# Revit family: Porecz_uchylna_dla_niepelnosprawnych_800 mm stal szlachetna matowa
name_source: partatom
category: Furniture
units: mm (PartAtom-declared; Revit-internal decimal feet)

## family parameters
Always vertical = Yes
Cut with Voids When Loaded = No
Host = Wall
Room Calculation Point = No
Shared = No

## types (1)
- S32UUWC8SNM
    Depth / Glebokosc = 800 mm  [stored 2.62467 ft]
    Description = Poręcz uchylna dla niepełnosprawnych to solidny, stabilny i bezpieczny pochwyt łazienkowy, który wykonano ze stali nierdzewnej. Matowe wykończenie ułatwia czyszczenie, a jednocześnie gwarantuje elegancki wygląd poręczy. Uchwyt o długości 80 cm  jest podporą dla ludzi z ograniczeniami ruchowymi podczas korzystania z urządzeń sanitarnych. Zwiększa on samodzielność i wygodę użytkowników. Odchylany do góry pochwyt posiada progresywny system hamulcowy, który zabezpiecza go przed niespodziewanym opadnięciem. Polecany jest do toalet w szpitalach, restauracjach, hotelach, szkołach, domach spokojnej starości i sanatoriach.
    Height / Wysokosc = 250 mm  [stored 0.82021 ft]
    Manufacturer = FANECO.com
    Manufacturer code / Kod producenta = 5901764294894
    Material = Stal nierdzewna AISI 316
    Material finish / Wykonczenie = Stal nierdzewna AISI 316
    Product code / Kod produktu = S32UUWC8SNM
    Type Comments = Poręcz uchylna dla niepełnosprawnych 800 mm stal szlachetna matowa
    URL = https://faneco.com
    Weight / Waga = 3 kg
    Width / Szerokosc = 120 mm  [stored 0.393701 ft]

note: [stored X ft] marks values corroborated as IEEE doubles in the binary element streams (Revit-internal decimal feet)

## geometry (parser evidence)
native form markers: Sweep x10
no freeform markers — native parametric forms only
